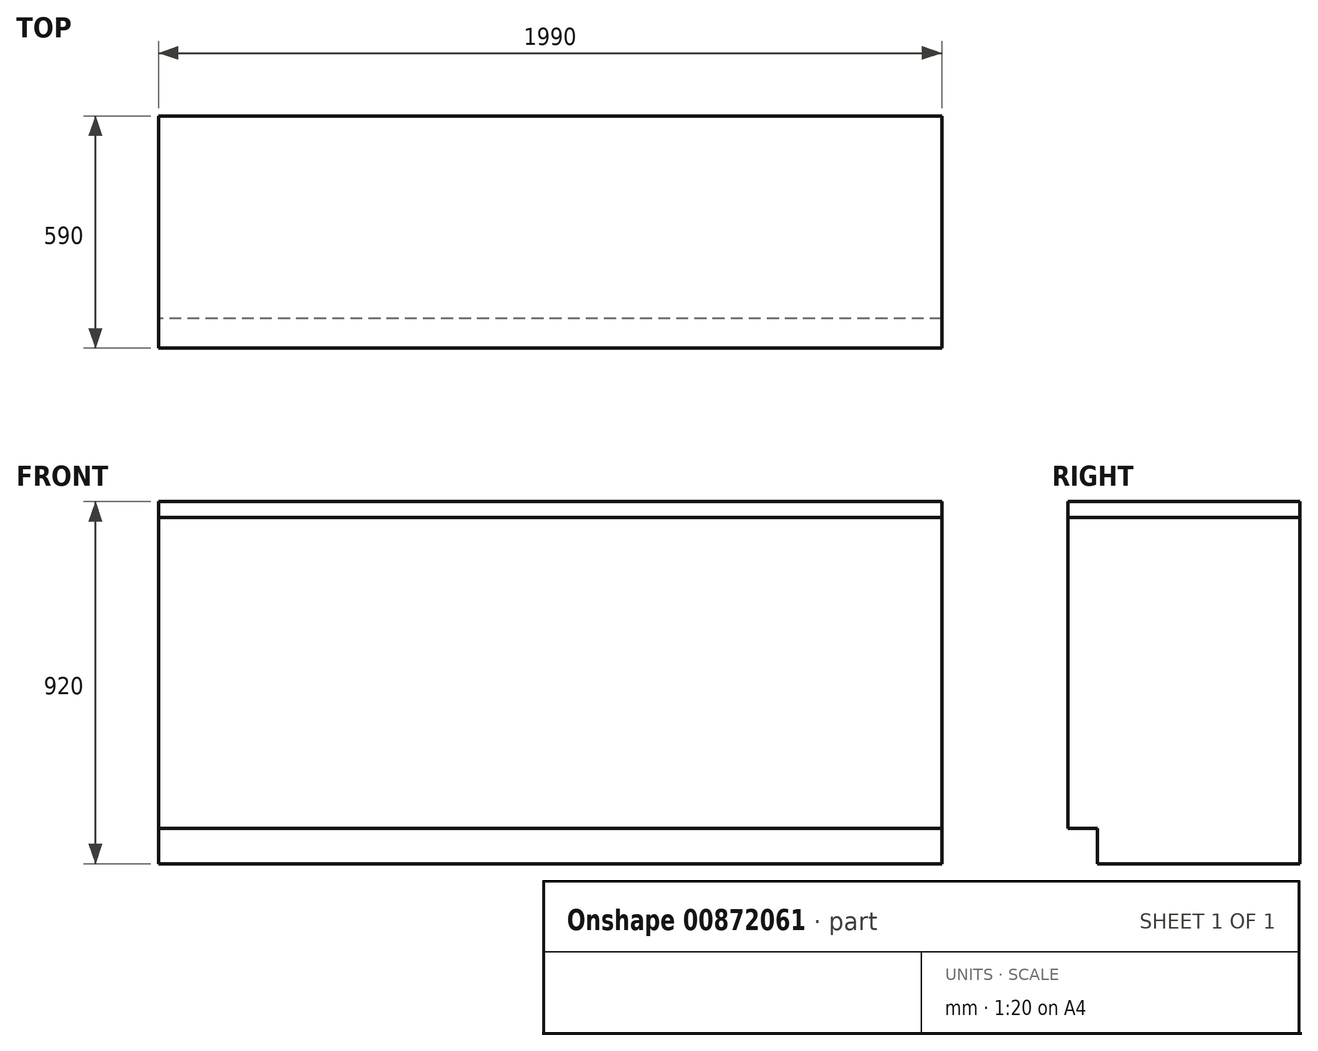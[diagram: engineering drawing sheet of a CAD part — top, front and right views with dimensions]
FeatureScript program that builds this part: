
annotation { "Feature Type Name" : "Feature", "Feature Type Description" : "" }
export const myFeature = defineFeature(function(context is Context, id is Id, definition is map)
    precondition{}
    {
        {
            var Q0;
            Q0=qCreatedBy(makeId("Top.planeOp"),FACE);
            var sketch = newSketch(context, id + "F0", { "sketchPlane" : qUnion([Q0])});
            skLineSegment(sketch, "E0.bottom", {"start": v(0, 0) * mm, "end": v(1990, 0) * mm});
            skLineSegment(sketch, "E0.top", {"start": v(0, 590) * mm, "end": v(1990, 590) * mm});
            skLineSegment(sketch, "E0.left", {"start": v(0, 0) * mm, "end": v(0, 590) * mm});
            skLineSegment(sketch, "E0.right", {"start": v(1990, 0) * mm, "end": v(1990, 590) * mm});
            skSolve(sketch);
        }
        {
            var Q0;
            Q0=qSketchRegion(id+"F0",true);
            extrude(context, id + "F1", {"entities" : qUnion([Q0]), "depth" : 880 * mm, "offsetDistance" : 25 * mm});
        }
        {
            var Q0;
            Q0=qCreatedBy(makeId("Right.planeOp"),FACE);
            var sketch = newSketch(context, id + "F2", { "sketchPlane" : qUnion([Q0])});
            skLineSegment(sketch, "E1.bottom", {"start": v(0, 0) * mm, "end": v(75, 0) * mm});
            skLineSegment(sketch, "E1.top", {"start": v(0, 90) * mm, "end": v(75, 90) * mm});
            skLineSegment(sketch, "E1.left", {"start": v(0, 0) * mm, "end": v(0, 90) * mm});
            skLineSegment(sketch, "E1.right", {"start": v(75, 0) * mm, "end": v(75, 90) * mm});
            skSolve(sketch);
        }
        {
            var Q0;
            Q0=qSketchRegion(id+"F2",true);
            extrude(context, id + "F3", {"entities" : qUnion([Q0]), "operationType" : NewBodyOperationType.REMOVE, "endBound" : BoundingType.THROUGH_ALL, "depth" : 25 * mm, "offsetDistance" : 25 * mm});
        }
        {
            var Q0;
            Q0=qCreatedBy(makeId("Right.planeOp"),FACE);
            var sketch = newSketch(context, id + "F4", { "sketchPlane" : qUnion([Q0])});
            skLineSegment(sketch, "E2.0", {"start": v(0, 880) * mm, "end": v(590, 880) * mm, "construction": true});
            skLineSegment(sketch, "E3.bottom", {"start": v(590, 880) * mm, "end": v(0, 880) * mm});
            skLineSegment(sketch, "E3.top", {"start": v(590, 920) * mm, "end": v(0, 920) * mm});
            skLineSegment(sketch, "E3.left", {"start": v(590, 880) * mm, "end": v(590, 920) * mm});
            skLineSegment(sketch, "E3.right", {"start": v(-50, 880) * mm, "end": v(-50, 920) * mm, "construction": true});
            skArc(sketch, "E4", {"start": v(-30, 920) * mm, "mid": v(-50, 900) * mm, "end": v(-30, 880) * mm, "construction": true});
            skLineSegment(sketch, "E5", {"start": v(550, 932.7) * mm, "end": v(550, 1040) * mm, "construction": true});
            skLineSegment(sketch, "E6", {"start": v(590, 1080) * mm, "end": v(590, 1080) * mm});
            skPoint(sketch, "E7.visualSharp", {"position": v(550, 1080) * mm});
            skArc(sketch, "E7.filletArc", {"start": v(590, 1080) * mm, "mid": v(561.72, 1068.28) * mm, "end": v(550, 1040) * mm, "construction": true});
            skPoint(sketch, "E8.newPointA", {"position": v(590, 920) * mm});
            skArc(sketch, "E8.filletArc", {"start": v(537.3, 920) * mm, "mid": v(546.28, 923.72) * mm, "end": v(550, 932.7) * mm, "construction": true});
            skLineSegment(sketch, "E9", {"start": v(0, 880) * mm, "end": v(0, 920) * mm});
            skSolve(sketch);
        }
        {
            var Q0;
            Q0=qSketchRegion(id+"F4",true);
            var Q1;
            Q1=makeQuery(id+"F1.opExtrude","SWEPT_FACE",FACE,{"disambiguationData":[OSD([sQuery(id+"F0.wireOp",EDGE,"E0.right")])]});
            extrude(context, id + "F5", {"entities" : qUnion([Q0]), "endBound" : BoundingType.UP_TO_SURFACE, "depth" : 25 * mm, "endBoundEntityFace" : qUnion([Q1]), "offsetDistance" : 25 * mm});
        }
    });
